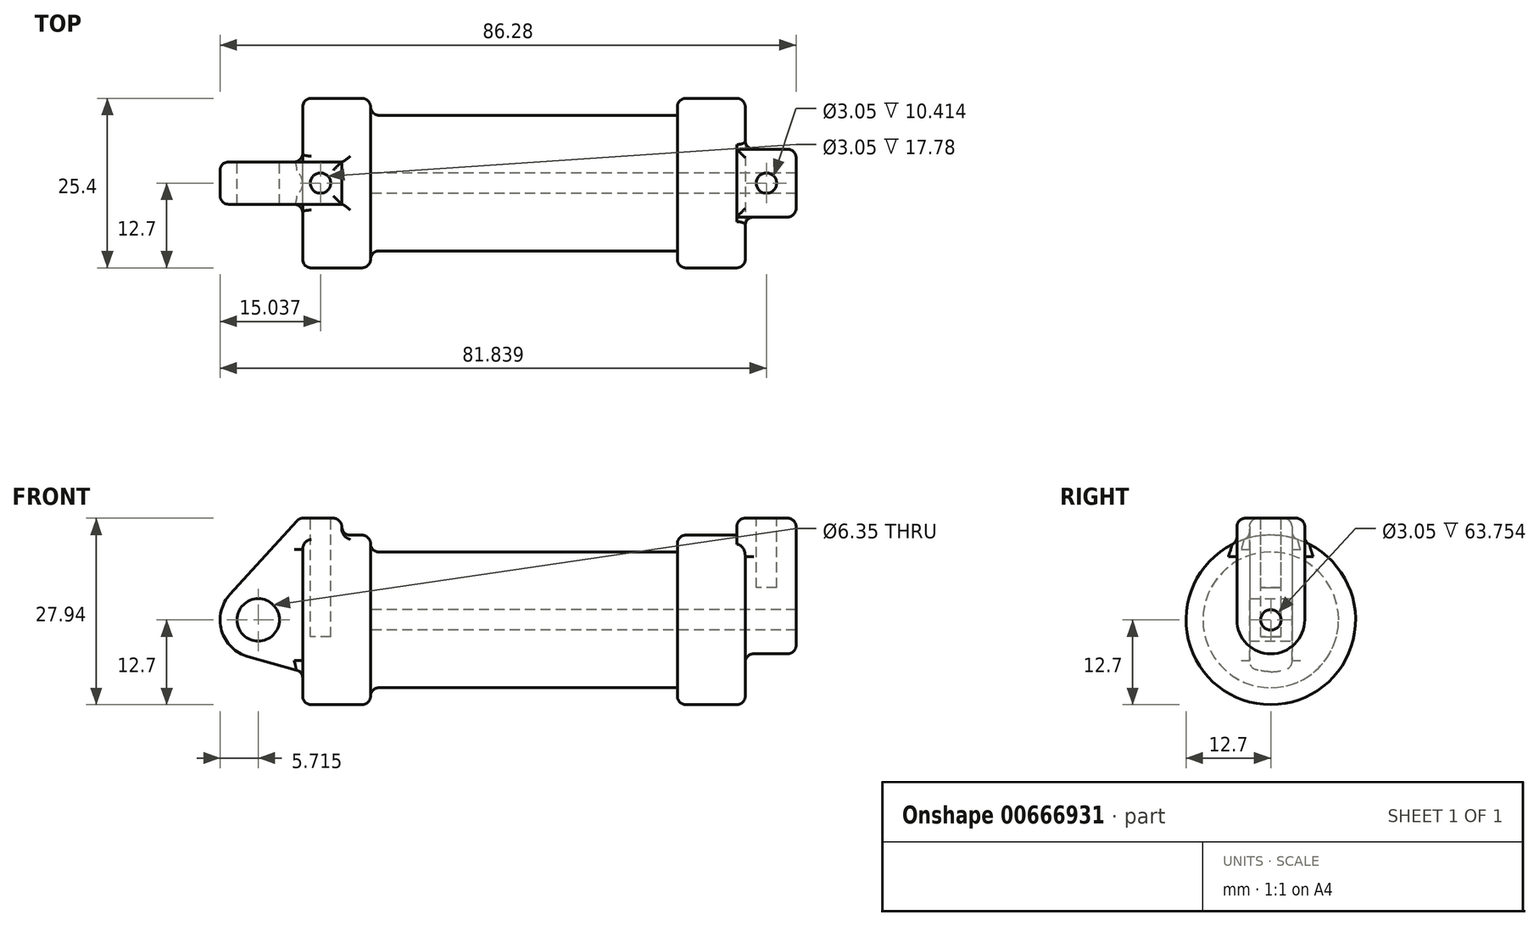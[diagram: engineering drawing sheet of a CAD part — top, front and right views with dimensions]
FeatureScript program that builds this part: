
annotation { "Feature Type Name" : "Feature", "Feature Type Description" : "" }
export const myFeature = defineFeature(function(context is Context, id is Id, definition is map)
    precondition{}
    {
        {
            var Q0;
            Q0=qCreatedBy(makeId("Front.planeOp"),FACE);
            var sketch = newSketch(context, id + "F0", { "sketchPlane" : qUnion([Q0])});
            skLineSegment(sketch, "E0", {"start": v(0, 0) * mm, "end": v(0, 12.7) * mm});
            skLineSegment(sketch, "E1", {"start": v(0, 12.7) * mm, "end": v(10.16, 12.7) * mm});
            skLineSegment(sketch, "E2", {"start": v(10.16, 12.7) * mm, "end": v(10.16, 10.16) * mm});
            skLineSegment(sketch, "E3", {"start": v(10.16, 10.16) * mm, "end": v(56.13, 10.16) * mm});
            skLineSegment(sketch, "E4", {"start": v(56.13, 10.16) * mm, "end": v(56.13, 12.7) * mm});
            skLineSegment(sketch, "E5", {"start": v(56.13, 12.7) * mm, "end": v(66.3, 12.7) * mm});
            skLineSegment(sketch, "E6", {"start": v(66.3, 12.7) * mm, "end": v(66.3, 0) * mm});
            skLineSegment(sketch, "E7", {"start": v(66.3, 0) * mm, "end": v(0, 0) * mm});
            skLineSegment(sketch, "E8", {"start": v(5.84, 15.24) * mm, "end": v(-0.5, 15.24) * mm});
            skLineSegment(sketch, "E9", {"start": v(-0.5, 15.24) * mm, "end": v(-10.88, 3.85) * mm});
            skLineSegment(sketch, "E10", {"start": v(0, 0) * mm, "end": v(-6.65, 0) * mm});
            skCircle(sketch, "E11", {"center": v(-6.65, 0) * mm, "radius": 5.72 * mm});
            skCircle(sketch, "E12", {"center": v(-6.65, 0) * mm, "radius": 3.18 * mm});
            skLineSegment(sketch, "E13", {"start": v(5.84, 15.24) * mm, "end": v(5.84, -9.4) * mm});
            skLineSegment(sketch, "E14", {"start": v(5.84, -9.4) * mm, "end": v(-8.18, -5.5) * mm});
            skSolve(sketch);
        }
        {
            var Q0;
            {var subQ0=sQuery(id+"F0.wireOp",EDGE,"E2");Q0=makeQuery(id+"F0.imprint","IMPRINT",FACE,{"disambiguationData":[TD([[makeQuery(id+"F0.imprint","IMPRINT",EDGE,{"derivedFrom":subQ0}),-1.0]])]});}
            var Q1;
            {var subQ0=sQuery(id+"F0.wireOp",EDGE,"E0");Q1=makeQuery(id+"F0.imprint","IMPRINT",FACE,{"disambiguationData":[TD([[makeQuery(id+"F0.imprint","IMPRINT",EDGE,{"derivedFrom":subQ0}),-1.0]])]});}
            var Q2;
            Q2=sQuery(id+"F0.wireOp",EDGE,"E7");
            revolve(context, id + "F1", {"entities" : qUnion([Q0, Q1]), "axis" : qUnion([Q2]), "revolveType" : RevolveType.FULL});
        }
        {
            var Q0;
            {var subQ1=sQuery(id+"F0.wireOp",EDGE,"E0");Q0=makeQuery(id+"F0.imprint","IMPRINT",FACE,{"disambiguationData":[TD([[makeQuery(id+"F0.imprint","IMPRINT",EDGE,{"derivedFrom":subQ1}),1.0]])]});}
            var Q1;
            {var subQ5=sQuery(id+"F0.wireOp",EDGE,"E12");Q1=makeQuery(id+"F0.imprint","IMPRINT",FACE,{"disambiguationData":[TD([[makeQuery(id+"F0.imprint","IMPRINT",EDGE,{"derivedFrom":subQ5}),-1.0]])]});}
            var Q2;
            {var subQ0=sQuery(id+"F0.wireOp",EDGE,"E0");Q2=makeQuery(id+"F0.imprint","IMPRINT",FACE,{"disambiguationData":[TD([[makeQuery(id+"F0.imprint","IMPRINT",EDGE,{"derivedFrom":subQ0}),-1.0]])]});}
            var Q3;
            {var subQ0=sQuery(id+"F0.wireOp",EDGE,"E14");Q3=makeQuery(id+"F0.imprint","IMPRINT",FACE,{"disambiguationData":[TD([[makeQuery(id+"F0.imprint","IMPRINT",EDGE,{"derivedFrom":subQ0}),-1.0]])]});}
            extrude(context, id + "F2", {"entities" : qUnion([Q0, Q1, Q2, Q3]), "operationType" : NewBodyOperationType.ADD, "endBound" : BoundingType.SYMMETRIC, "depth" : 6.35 * mm, "offsetDistance" : 25.4 * mm});
        }
        {
            var Q0;
            Q0=makeQuery(id+"F1.opRevolve","SWEPT_FACE",FACE,{"disambiguationData":[OSD([sQuery(id+"F0.wireOp",EDGE,"E6")])]});
            var sketch = newSketch(context, id + "F3", { "sketchPlane" : qUnion([Q0])});
            skCircle(sketch, "E15", {"center": v(0, 0) * mm, "radius": 1.52 * mm});
            skCircle(sketch, "E16", {"center": v(0, 0) * mm, "radius": 5.08 * mm});
            skLineSegment(sketch, "E17", {"start": v(5.08, 0) * mm, "end": v(5.08, 15.24) * mm});
            skLineSegment(sketch, "E18", {"start": v(-5.08, 0) * mm, "end": v(-5.08, 15.24) * mm});
            skLineSegment(sketch, "E19", {"start": v(-5.08, 15.24) * mm, "end": v(5.08, 15.24) * mm});
            skSolve(sketch);
        }
        {
            var Q0;
            {var subQ0=sQuery(id+"F3.wireOp",EDGE,"E19");Q0=makeQuery(id+"F3.imprint","IMPRINT",FACE,{"disambiguationData":[TD([[makeQuery(id+"F3.imprint","IMPRINT",EDGE,{"derivedFrom":subQ0}),-1.0]])]});}
            var Q1;
            {var subQ0=sQuery(id+"F3.wireOp",EDGE,"E17");var subQ1=sQuery(id+"F3.wireOp",EDGE,"E16");var subQ2=makeQuery(id+"F3.imprint","INTERSECT",VERTEX,{"derivedFrom":[subQ1,subQ0]});Q1=makeQuery(id+"F3.imprint","IMPRINT",FACE,{"disambiguationData":[TD([[makeQuery(id+"F3.imprint","IMPRINT",EDGE,{"disambiguationData":[TD([[subQ2,-1.0]])],"derivedFrom":subQ1}),-1.0]])]});}
            var Q2;
            Q2=makeQuery(id+"F3.imprint","IMPRINT",FACE,{"disambiguationData":[TD([[makeQuery(id+"F3.imprint","IMPRINT",EDGE,{"derivedFrom":sQuery(id+"F3.wireOp",EDGE,"E15")}),-1.0]])]});
            extrude(context, id + "F4", {"entities" : qUnion([Q0, Q1, Q2]), "operationType" : NewBodyOperationType.ADD, "depth" : 7.62 * mm, "offsetDistance" : 25.4 * mm});
        }
        {
            var Q0;
            Q0=makeQuery(id+"F4.opExtrude","CAP_FACE",FACE,{"disambiguationData":[OSD([sQuery(id+"F3.wireOp",EDGE,"E15"),sQuery(id+"F3.wireOp",EDGE,"E16"),sQuery(id+"F3.wireOp",EDGE,"E17"),sQuery(id+"F3.wireOp",EDGE,"E18"),sQuery(id+"F3.wireOp",EDGE,"E19")])],"isStart":true});
            var Q1;
            Q1=makeQuery(id+"F4.opExtrude","CAP_FACE",FACE,{"disambiguationData":[OSD([sQuery(id+"F3.wireOp",EDGE,"E15"),sQuery(id+"F3.wireOp",EDGE,"E16"),sQuery(id+"F3.wireOp",EDGE,"E17"),sQuery(id+"F3.wireOp",EDGE,"E18"),sQuery(id+"F3.wireOp",EDGE,"E19")])],"isStart":false});
            extrude(context, id + "F5", {"entities" : qUnion([Q0, Q1]), "operationType" : NewBodyOperationType.ADD, "depth" : 1.27 * mm, "offsetDistance" : 25.4 * mm});
        }
        {
            var Q0;
            Q0=makeQuery(id+"F4.boolean.opBoolean","SPLIT",FACE,{"disambiguationData":[TD([makeQuery(id+"F4.opExtrude","SWEPT_FACE",FACE,{"disambiguationData":[OSD([sQuery(id+"F3.wireOp",EDGE,"E15")])]})])],"derivedFrom":makeQuery(id+"F1.opRevolve","SWEPT_FACE",FACE,{"disambiguationData":[OSD([sQuery(id+"F0.wireOp",EDGE,"E6")])]})});
            var Q1;
            Q1=makeQuery(id+"F1.opRevolve","SWEPT_FACE",FACE,{"disambiguationData":[OSD([sQuery(id+"F0.wireOp",EDGE,"E2")])]});
            extrude(context, id + "F6", {"entities" : qUnion([Q0]), "operationType" : NewBodyOperationType.REMOVE, "endBound" : BoundingType.UP_TO_SURFACE, "oppositeDirection" : true, "depth" : 25.4 * mm, "endBoundEntityFace" : qUnion([Q1]), "offsetDistance" : 25.4 * mm});
        }
        {
            var Q0;
            {var subQ0=sQuery(id+"F3.wireOp",EDGE,"E19");Q0=makeQuery(id+"F5.boolean.opBoolean","MERGE",FACE,{"derivedFrom":[makeQuery(id+"F4.opExtrude","SWEPT_FACE",FACE,{"disambiguationData":[OSD([subQ0])]}),makeQuery(id+"F5.opExtrude","SWEPT_FACE",FACE,{"disambiguationData":[OSD([subQ0]),TDD([makeQuery(id+"F4.opExtrude","CAP_EDGE",EDGE,{"disambiguationData":[OSD([subQ0])],"isStart":true})])]})]});}
            var sketch = newSketch(context, id + "F7", { "sketchPlane" : qUnion([Q0])});
            skCircle(sketch, "E20", {"center": v(69.47, 0) * mm, "radius": 1.52 * mm});
            skPoint(sketch, "E21", {"position": v(73.91, 0) * mm});
            skPoint(sketch, "E22", {"position": v(65.02, 0) * mm});
            skPoint(sketch, "E23", {"position": v(69.47, 5.08) * mm});
            skPoint(sketch, "E24", {"position": v(69.47, -5.08) * mm});
            skSolve(sketch);
        }
        {
            var Q0;
            Q0=makeQuery(id+"F7.imprint","IMPRINT",FACE,{"disambiguationData":[TD([[makeQuery(id+"F7.imprint","IMPRINT",EDGE,{"derivedFrom":sQuery(id+"F7.wireOp",EDGE,"E20")}),1.0]])]});
            extrude(context, id + "F8", {"entities" : qUnion([Q0]), "operationType" : NewBodyOperationType.REMOVE, "oppositeDirection" : true, "depth" : 10.4 * mm, "offsetDistance" : 25.4 * mm});
        }
        {
            var Q0;
            Q0=makeQuery(id+"F2.opExtrude","SWEPT_FACE",FACE,{"disambiguationData":[OSD([sQuery(id+"F0.wireOp",EDGE,"E8")])]});
            var sketch = newSketch(context, id + "F9", { "sketchPlane" : qUnion([Q0])});
            skCircle(sketch, "E25", {"center": v(2.67, 0) * mm, "radius": 1.52 * mm});
            skPoint(sketch, "E26", {"position": v(5.84, 0) * mm});
            skPoint(sketch, "E27", {"position": v(-0.5, 0) * mm});
            skPoint(sketch, "E28", {"position": v(2.67, -3.18) * mm});
            skSolve(sketch);
        }
        {
            var Q0;
            Q0=makeQuery(id+"F9.imprint","IMPRINT",FACE,{"disambiguationData":[TD([[makeQuery(id+"F9.imprint","IMPRINT",EDGE,{"derivedFrom":sQuery(id+"F9.wireOp",EDGE,"E25")}),1.0]])]});
            extrude(context, id + "F10", {"entities" : qUnion([Q0]), "operationType" : NewBodyOperationType.REMOVE, "oppositeDirection" : true, "depth" : 17.78 * mm, "offsetDistance" : 25.4 * mm});
        }
        {
            var Q0;
            {var subQ0=sQuery(id+"F0.wireOp",EDGE,"E5");var subQ1=sQuery(id+"F0.wireOp",EDGE,"E6");Q0=makeQuery(id+"F4.boolean.opBoolean","SPLIT",EDGE,{"disambiguationData":[topologyDisambiguationEdgeConnected([makeQuery(id+"F1.opRevolve","SWEPT_FACE",FACE,{"disambiguationData":[OSD([subQ1])]})])],"derivedFrom":makeQuery(id+"F1.opRevolve","SWEPT_EDGE",EDGE,{"disambiguationData":[OSD([subQ0,subQ1])]})});}
            var Q1;
            Q1=makeQuery(id+"F1.opRevolve","SWEPT_EDGE",EDGE,{"disambiguationData":[OSD([sQuery(id+"F0.wireOp",EDGE,"E4"),sQuery(id+"F0.wireOp",EDGE,"E5")])]});
            var Q2;
            Q2=makeQuery(id+"F1.opRevolve","SWEPT_EDGE",EDGE,{"disambiguationData":[OSD([sQuery(id+"F0.wireOp",EDGE,"E1"),sQuery(id+"F0.wireOp",EDGE,"E2")])]});
            var Q3;
            Q3=makeQuery(id+"F1.opRevolve","SWEPT_EDGE",EDGE,{"disambiguationData":[OSD([sQuery(id+"F0.wireOp",EDGE,"E0"),sQuery(id+"F0.wireOp",EDGE,"E1")])]});
            fillet(context, id + "F11", {"entities" : qUnion([Q0, Q1, Q2, Q3]), "radius" : 1.27 * mm, "tangentPropagation" : true, "allowEdgeOverflow" : false});
        }
        {
            var Q0;
            Q0=makeQuery(id+"F1.opRevolve","SWEPT_EDGE",EDGE,{"disambiguationData":[OSD([sQuery(id+"F0.wireOp",EDGE,"E2"),sQuery(id+"F0.wireOp",EDGE,"E3")])]});
            var Q1;
            Q1=makeQuery(id+"F2.opExtrude","SWEPT_EDGE",EDGE,{"disambiguationData":[OSD([sQuery(id+"F0.wireOp",EDGE,"E8"),sQuery(id+"F0.wireOp",EDGE,"E13")])]});
            var Q2;
            Q2=makeQuery(id+"F2.opExtrude","CAP_EDGE",EDGE,{"disambiguationData":[OSD([sQuery(id+"F0.wireOp",EDGE,"E8")])],"isStart":false});
            var Q3;
            Q3=makeQuery(id+"F2.opExtrude","CAP_EDGE",EDGE,{"disambiguationData":[OSD([sQuery(id+"F0.wireOp",EDGE,"E8")])],"isStart":true});
            var Q4;
            Q4=makeQuery(id+"F2.opExtrude","SWEPT_EDGE",EDGE,{"disambiguationData":[OSD([sQuery(id+"F0.wireOp",EDGE,"E8"),sQuery(id+"F0.wireOp",EDGE,"E9")])]});
            var Q5;
            Q5=makeQuery(id+"F2.boolean.opBoolean","INTERSECT",EDGE,{"derivedFrom":[makeQuery(id+"F1.opRevolve","SWEPT_FACE",FACE,{"disambiguationData":[OSD([sQuery(id+"F0.wireOp",EDGE,"E1")])]}),makeQuery(id+"F2.opExtrude","SWEPT_FACE",FACE,{"disambiguationData":[OSD([sQuery(id+"F0.wireOp",EDGE,"E13")])]})]});
            var Q6;
            Q6=makeQuery(id+"F2.boolean.opBoolean","INTERSECT",EDGE,{"derivedFrom":[makeQuery(id+"F1.opRevolve","SWEPT_FACE",FACE,{"disambiguationData":[OSD([sQuery(id+"F0.wireOp",EDGE,"E1")])]}),makeQuery(id+"F2.opExtrude","CAP_FACE",FACE,{"disambiguationData":[OSD([sQuery(id+"F0.wireOp",EDGE,"E8"),sQuery(id+"F0.wireOp",EDGE,"E9"),sQuery(id+"F0.wireOp",EDGE,"E11"),sQuery(id+"F0.wireOp",EDGE,"E12"),sQuery(id+"F0.wireOp",EDGE,"E13"),sQuery(id+"F0.wireOp",EDGE,"E14")])],"isStart":false})]});
            var Q7;
            Q7=makeQuery(id+"F2.boolean.opBoolean","INTERSECT",EDGE,{"derivedFrom":[makeQuery(id+"F1.opRevolve","SWEPT_FACE",FACE,{"disambiguationData":[OSD([sQuery(id+"F0.wireOp",EDGE,"E1")])]}),makeQuery(id+"F2.opExtrude","CAP_FACE",FACE,{"disambiguationData":[OSD([sQuery(id+"F0.wireOp",EDGE,"E8"),sQuery(id+"F0.wireOp",EDGE,"E9"),sQuery(id+"F0.wireOp",EDGE,"E11"),sQuery(id+"F0.wireOp",EDGE,"E12"),sQuery(id+"F0.wireOp",EDGE,"E13"),sQuery(id+"F0.wireOp",EDGE,"E14")])],"isStart":true})]});
            var Q8;
            Q8=makeQuery(id+"F2.opExtrude","CAP_EDGE",EDGE,{"disambiguationData":[OSD([sQuery(id+"F0.wireOp",EDGE,"E9")])],"isStart":true});
            var Q9;
            Q9=makeQuery(id+"F2.opExtrude","CAP_EDGE",EDGE,{"disambiguationData":[OSD([sQuery(id+"F0.wireOp",EDGE,"E9")])],"isStart":false});
            fillet(context, id + "F12", {"entities" : qUnion([Q0, Q1, Q2, Q3, Q4, Q5, Q6, Q7, Q8, Q9]), "radius" : 1.27 * mm, "tangentPropagation" : true, "allowEdgeOverflow" : false});
        }
        {
            var Q0;
            Q0=makeQuery(id+"F5.opExtrude","CAP_EDGE",EDGE,{"disambiguationData":[OSD([sQuery(id+"F0.wireOp",EDGE,"E5"),sQuery(id+"F0.wireOp",EDGE,"E6")])],"isStart":false});
            var Q1;
            {var subQ0=sQuery(id+"F3.wireOp",EDGE,"E18");Q1=makeQuery(id+"F4.boolean.opBoolean","SPLIT",EDGE,{"disambiguationData":[topologyDisambiguationEdgeConnected([makeQuery(id+"F1.opRevolve","SWEPT_FACE",FACE,{"disambiguationData":[OSD([sQuery(id+"F0.wireOp",EDGE,"E6")])]})])],"derivedFrom":makeQuery(id+"F4.opExtrude","CAP_EDGE",EDGE,{"disambiguationData":[OSD([subQ0])],"isStart":true})});}
            var Q2;
            Q2=makeQuery(id+"F4.opExtrude","CAP_EDGE",EDGE,{"disambiguationData":[OSD([sQuery(id+"F3.wireOp",EDGE,"E18")])],"isStart":false});
            var Q3;
            {var subQ0=sQuery(id+"F3.wireOp",EDGE,"E19");var subQ1=sQuery(id+"F3.wireOp",EDGE,"E18");Q3=makeQuery(id+"F5.boolean.opBoolean","MERGE",EDGE,{"derivedFrom":[makeQuery(id+"F4.opExtrude","SWEPT_EDGE",EDGE,{"disambiguationData":[OSD([subQ1,subQ0])]}),makeQuery(id+"F5.opExtrude","SWEPT_EDGE",EDGE,{"disambiguationData":[OSD([subQ1,subQ0]),TDD([makeQuery(id+"F4.opExtrude","CAP_VERTEX",VERTEX,{"disambiguationData":[OSD([subQ1,subQ0])],"isStart":true})])]})]});}
            var Q4;
            Q4=makeQuery(id+"F4.opExtrude","CAP_EDGE",EDGE,{"disambiguationData":[OSD([sQuery(id+"F3.wireOp",EDGE,"E19")])],"isStart":false});
            var Q5;
            {var subQ0=sQuery(id+"F3.wireOp",EDGE,"E19");var subQ1=sQuery(id+"F3.wireOp",EDGE,"E17");Q5=makeQuery(id+"F5.boolean.opBoolean","MERGE",EDGE,{"derivedFrom":[makeQuery(id+"F4.opExtrude","SWEPT_EDGE",EDGE,{"disambiguationData":[OSD([subQ1,subQ0])]}),makeQuery(id+"F5.opExtrude","SWEPT_EDGE",EDGE,{"disambiguationData":[OSD([subQ1,subQ0]),TDD([makeQuery(id+"F4.opExtrude","CAP_VERTEX",VERTEX,{"disambiguationData":[OSD([subQ1,subQ0])],"isStart":true})])]})]});}
            var Q6;
            {var subQ0=sQuery(id+"F3.wireOp",EDGE,"E19");Q6=makeQuery(id+"F5.opExtrude","CAP_EDGE",EDGE,{"disambiguationData":[OSD([subQ0]),TDD([makeQuery(id+"F4.opExtrude","CAP_EDGE",EDGE,{"disambiguationData":[OSD([subQ0])],"isStart":true})])],"isStart":false});}
            fillet(context, id + "F13", {"entities" : qUnion([Q0, Q1, Q2, Q3, Q4, Q5, Q6]), "radius" : 1.27 * mm, "tangentPropagation" : true, "allowEdgeOverflow" : false});
        }
    });
